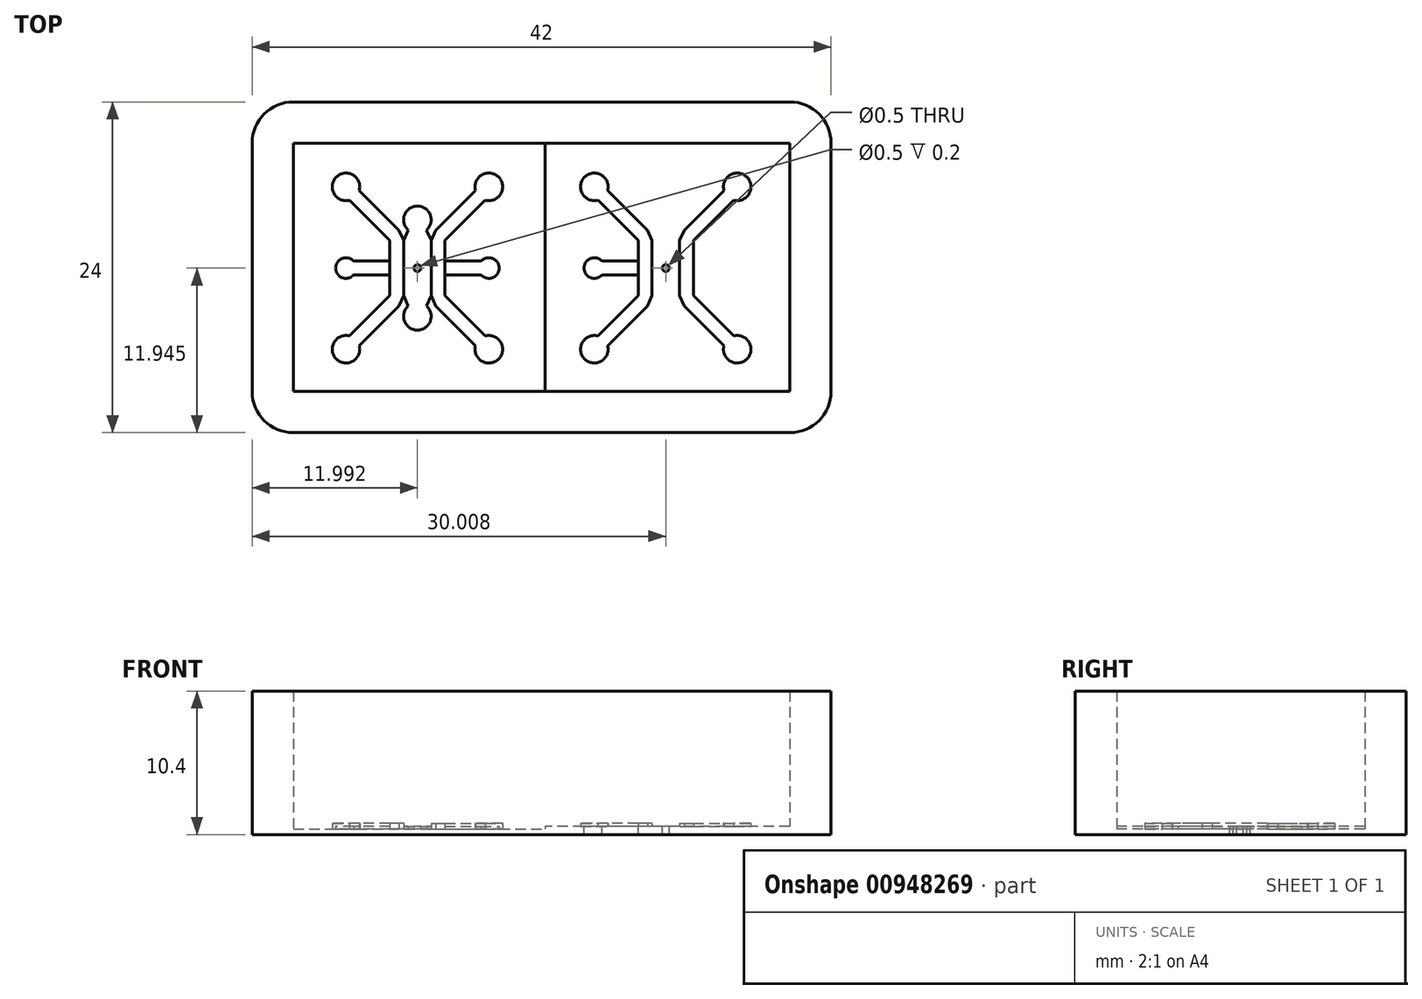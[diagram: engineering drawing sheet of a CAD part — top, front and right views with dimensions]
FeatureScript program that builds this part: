
annotation { "Feature Type Name" : "Feature", "Feature Type Description" : "" }
export const myFeature = defineFeature(function(context is Context, id is Id, definition is map)
    precondition{}
    {
        {
            var Q0;
            Q0=qCreatedBy(makeId("Top.planeOp"),FACE);
            var sketch = newSketch(context, id + "F0", { "sketchPlane" : qUnion([Q0])});
            skLineSegment(sketch, "E0.right", {"start": v(10, 8.95) * mm, "end": v(10, 10.95) * mm});
            skLineSegment(sketch, "E1.MirrorCS", {"start": v(8, 8.95) * mm, "end": v(8, 10.95) * mm});
            skLineSegment(sketch, "E2.MirrorCS", {"start": v(10, 8.95) * mm, "end": v(10, 6.95) * mm});
            skLineSegment(sketch, "E3.MirrorCS", {"start": v(8, 8.95) * mm, "end": v(8, 6.95) * mm});
            skLineSegment(sketch, "E4", {"start": v(9.65, 6.2) * mm, "end": v(10, 6.95) * mm});
            skLineSegment(sketch, "E5", {"start": v(8, 6.95) * mm, "end": v(8.33, 6.2) * mm});
            skCircle(sketch, "E6", {"center": v(9, 8.95) * mm, "radius": 0.25 * mm});
            skArc(sketch, "E7", {"start": v(8.33, 6.2) * mm, "mid": v(9, 4.45) * mm, "end": v(9.65, 6.2) * mm});
            skLineSegment(sketch, "E8.left", {"start": v(10, 10.95) * mm, "end": v(10, 8.95) * mm});
            skLineSegment(sketch, "E8.right", {"start": v(11, 10.95) * mm, "end": v(11, 8.95) * mm});
            skLineSegment(sketch, "E9.MirrorCS", {"start": v(11, 6.95) * mm, "end": v(11, 8.95) * mm});
            skLineSegment(sketch, "E10", {"start": v(10, 6.95) * mm, "end": v(10.33, 6.2) * mm});
            skLineSegment(sketch, "E11", {"start": v(10.33, 6.2) * mm, "end": v(11, 5.53) * mm});
            skLineSegment(sketch, "E12", {"start": v(11, 5.53) * mm, "end": v(13.2, 3.32) * mm});
            skArc(sketch, "E13", {"start": v(13.2, 3.32) * mm, "mid": v(14.88, 2.35) * mm, "end": v(13.92, 4.02) * mm});
            skArc(sketch, "E14.MirrorCS", {"start": v(8.33, 11.7) * mm, "mid": v(9, 13.45) * mm, "end": v(9.65, 11.7) * mm});
            skLineSegment(sketch, "E15.MirrorCS", {"start": v(9.65, 11.7) * mm, "end": v(10, 10.95) * mm});
            skLineSegment(sketch, "E16.MirrorCS", {"start": v(8, 10.95) * mm, "end": v(8.33, 11.7) * mm});
            skLineSegment(sketch, "E17.MirrorCS", {"start": v(10, 10.95) * mm, "end": v(10.33, 11.7) * mm});
            skLineSegment(sketch, "E18.MirrorCS", {"start": v(10.33, 11.7) * mm, "end": v(11, 12.36) * mm});
            skLineSegment(sketch, "E19.MirrorCS", {"start": v(11, 12.36) * mm, "end": v(13.2, 14.58) * mm});
            skArc(sketch, "E20.MirrorCS", {"start": v(13.2, 14.58) * mm, "mid": v(14.88, 15.54) * mm, "end": v(13.92, 13.87) * mm});
            skLineSegment(sketch, "E21", {"start": v(11, 6.95) * mm, "end": v(13.92, 4.02) * mm});
            skLineSegment(sketch, "E22.MirrorCS", {"start": v(11, 10.95) * mm, "end": v(13.92, 13.87) * mm});
            skLineSegment(sketch, "E23.MirrorCS", {"start": v(8, 10.95) * mm, "end": v(7.65, 11.7) * mm});
            skLineSegment(sketch, "E24.MirrorCS", {"start": v(8, 6.95) * mm, "end": v(7.65, 6.2) * mm});
            skLineSegment(sketch, "E25.MirrorCS", {"start": v(7.65, 11.7) * mm, "end": v(7, 12.36) * mm});
            skLineSegment(sketch, "E26.MirrorCS", {"start": v(7, 12.36) * mm, "end": v(4.78, 14.58) * mm});
            skArc(sketch, "E27.MirrorCS", {"start": v(4.78, 14.58) * mm, "mid": v(3.1, 15.54) * mm, "end": v(4.07, 13.87) * mm});
            skLineSegment(sketch, "E28.MirrorCS", {"start": v(7, 10.95) * mm, "end": v(4.07, 13.87) * mm});
            skLineSegment(sketch, "E29.MirrorCS", {"start": v(7, 10.95) * mm, "end": v(7, 8.95) * mm});
            skLineSegment(sketch, "E30.MirrorCS", {"start": v(7, 6.95) * mm, "end": v(7, 8.95) * mm});
            skArc(sketch, "E31.MirrorCS", {"start": v(4.78, 3.32) * mm, "mid": v(3.1, 2.35) * mm, "end": v(4.07, 4.02) * mm});
            skLineSegment(sketch, "E32.MirrorCS", {"start": v(7, 6.95) * mm, "end": v(4.07, 4.02) * mm});
            skLineSegment(sketch, "E33.MirrorCS", {"start": v(7, 5.53) * mm, "end": v(4.78, 3.32) * mm});
            skLineSegment(sketch, "E34.MirrorCS", {"start": v(7.65, 6.2) * mm, "end": v(7, 5.53) * mm});
            skLineSegment(sketch, "E35", {"start": v(11, 9.45) * mm, "end": v(13.61, 9.45) * mm});
            skLineSegment(sketch, "E36", {"start": v(11, 8.45) * mm, "end": v(13.61, 8.45) * mm});
            skArc(sketch, "E37", {"start": v(13.8, 9.6) * mm, "mid": v(13.7, 9.53) * mm, "end": v(13.61, 9.45) * mm});
            skArc(sketch, "E38", {"start": v(13.61, 8.45) * mm, "mid": v(14.91, 8.82) * mm, "end": v(13.8, 9.6) * mm});
            skLineSegment(sketch, "E39.MirrorCS", {"start": v(7, 9.45) * mm, "end": v(4.37, 9.45) * mm});
            skLineSegment(sketch, "E40.MirrorCS", {"start": v(7, 8.45) * mm, "end": v(4.37, 8.45) * mm});
            skArc(sketch, "E41.MirrorCS", {"start": v(4.37, 8.45) * mm, "mid": v(3.07, 8.82) * mm, "end": v(4.18, 9.6) * mm});
            skArc(sketch, "E42.MirrorCS", {"start": v(4.18, 9.6) * mm, "mid": v(4.28, 9.53) * mm, "end": v(4.37, 9.45) * mm});
            skPoint(sketch, "E43.startSnap0", {"position": v(15, 8.95) * mm});
            skPoint(sketch, "E43.startSnap1", {"position": v(14.91, 8.82) * mm});
            skPoint(sketch, "E43.endSnap0", {"position": v(14.91, 8.82) * mm});
            skPoint(sketch, "E44.visualSharp", {"position": v(0, 18) * mm});
            skPoint(sketch, "E45.visualSharp", {"position": v(0, 0) * mm});
            skLineSegment(sketch, "E46", {"start": v(9, 12.45) * mm, "end": v(9, 5.45) * mm});
            skLineSegment(sketch, "E47.bottom", {"start": v(0, 18) * mm, "end": v(18, 18) * mm});
            skLineSegment(sketch, "E47.top", {"start": v(0, 0) * mm, "end": v(18, 0) * mm});
            skLineSegment(sketch, "E47.left", {"start": v(0, 18) * mm, "end": v(0, 0) * mm});
            skLineSegment(sketch, "E47.right", {"start": v(18, 18) * mm, "end": v(18, 0) * mm});
            skLineSegment(sketch, "E48", {"start": v(21.4, 0) * mm, "end": v(21.4, 0) * mm});
            skLineSegment(sketch, "E49.MirrorCS", {"start": v(36, 18) * mm, "end": v(36, 0) * mm});
            skPoint(sketch, "E50.MirrorP", {"position": v(36, 0) * mm});
            skLineSegment(sketch, "E51.MirrorCS", {"start": v(36, 18) * mm, "end": v(18, 18) * mm});
            skPoint(sketch, "E52.MirrorP", {"position": v(36, 18) * mm});
            skLineSegment(sketch, "E53.MirrorCS", {"start": v(14.6, 0) * mm, "end": v(14.6, 0) * mm});
            skLineSegment(sketch, "E54.MirrorCS", {"start": v(36, 0) * mm, "end": v(18, 0) * mm});
            skPoint(sketch, "E55.MirrorP", {"position": v(21.09, 8.82) * mm});
            skLineSegment(sketch, "E56.MirrorCS", {"start": v(28, 10.95) * mm, "end": v(27.67, 11.7) * mm});
            skLineSegment(sketch, "E57.MirrorCS", {"start": v(26, 6.95) * mm, "end": v(25.67, 6.2) * mm});
            skLineSegment(sketch, "E58.MirrorCS", {"start": v(26, 8.95) * mm, "end": v(26, 10.95) * mm});
            skLineSegment(sketch, "E59.MirrorCS", {"start": v(28.35, 6.2) * mm, "end": v(29, 5.53) * mm});
            skArc(sketch, "E60.MirrorCS", {"start": v(31.82, 9.6) * mm, "mid": v(31.72, 9.53) * mm, "end": v(31.63, 9.45) * mm});
            skArc(sketch, "E61.MirrorCS", {"start": v(22.2, 9.6) * mm, "mid": v(22.3, 9.53) * mm, "end": v(22.39, 9.45) * mm});
            skLineSegment(sketch, "E62.MirrorCS", {"start": v(25.67, 11.7) * mm, "end": v(25, 12.36) * mm});
            skLineSegment(sketch, "E63.MirrorCS", {"start": v(28, 10.95) * mm, "end": v(28.35, 11.7) * mm});
            skLineSegment(sketch, "E64.MirrorCS", {"start": v(26, 10.95) * mm, "end": v(25.67, 11.7) * mm});
            skLineSegment(sketch, "E65.MirrorCS", {"start": v(26.35, 11.7) * mm, "end": v(26, 10.95) * mm});
            skLineSegment(sketch, "E66.MirrorCS", {"start": v(28.35, 11.7) * mm, "end": v(29, 12.36) * mm});
            skLineSegment(sketch, "E67.MirrorCS", {"start": v(25.67, 6.2) * mm, "end": v(25, 5.53) * mm});
            skLineSegment(sketch, "E68.MirrorCS", {"start": v(28, 6.95) * mm, "end": v(27.67, 6.2) * mm});
            skLineSegment(sketch, "E69.MirrorCS", {"start": v(28, 6.95) * mm, "end": v(28.35, 6.2) * mm});
            skArc(sketch, "E70.MirrorCS", {"start": v(22.39, 8.45) * mm, "mid": v(21.09, 8.82) * mm, "end": v(22.2, 9.6) * mm});
            skLineSegment(sketch, "E71.MirrorCS", {"start": v(26.35, 6.2) * mm, "end": v(26, 6.95) * mm});
            skPoint(sketch, "E72.MirrorP", {"position": v(21, 8.95) * mm});
            skCircle(sketch, "E73.MirrorC", {"center": v(27, 8.95) * mm, "radius": 0.25 * mm});
            skLineSegment(sketch, "E74.MirrorCS", {"start": v(28, 8.95) * mm, "end": v(28, 10.95) * mm});
            skArc(sketch, "E75.MirrorCS", {"start": v(22.8, 14.58) * mm, "mid": v(21.12, 15.54) * mm, "end": v(22.08, 13.87) * mm});
            skLineSegment(sketch, "E76.MirrorCS", {"start": v(29, 9.45) * mm, "end": v(31.63, 9.45) * mm});
            skLineSegment(sketch, "E77.MirrorCS", {"start": v(29, 6.95) * mm, "end": v(31.93, 4.02) * mm});
            skLineSegment(sketch, "E78.MirrorCS", {"start": v(25, 5.53) * mm, "end": v(22.8, 3.32) * mm});
            skLineSegment(sketch, "E79.MirrorCS", {"start": v(27, 12.45) * mm, "end": v(27, 5.45) * mm});
            skLineSegment(sketch, "E80.MirrorCS", {"start": v(29, 12.36) * mm, "end": v(31.22, 14.58) * mm});
            skLineSegment(sketch, "E81.MirrorCS", {"start": v(29, 6.95) * mm, "end": v(29, 8.95) * mm});
            skLineSegment(sketch, "E82.MirrorCS", {"start": v(29, 5.53) * mm, "end": v(31.22, 3.32) * mm});
            skLineSegment(sketch, "E83.MirrorCS", {"start": v(29, 8.45) * mm, "end": v(31.63, 8.45) * mm});
            skLineSegment(sketch, "E84.MirrorCS", {"start": v(29, 10.95) * mm, "end": v(29, 8.95) * mm});
            skLineSegment(sketch, "E85.MirrorCS", {"start": v(25, 12.36) * mm, "end": v(22.8, 14.58) * mm});
            skLineSegment(sketch, "E86.MirrorCS", {"start": v(26, 10.95) * mm, "end": v(26, 8.95) * mm});
            skArc(sketch, "E87.MirrorCS", {"start": v(31.63, 8.45) * mm, "mid": v(32.93, 8.82) * mm, "end": v(31.82, 9.6) * mm});
            skLineSegment(sketch, "E88.MirrorCS", {"start": v(29, 10.95) * mm, "end": v(31.93, 13.87) * mm});
            skLineSegment(sketch, "E89.MirrorCS", {"start": v(28, 8.95) * mm, "end": v(28, 6.95) * mm});
            skLineSegment(sketch, "E90.MirrorCS", {"start": v(25, 6.95) * mm, "end": v(25, 8.95) * mm});
            skArc(sketch, "E91.MirrorCS", {"start": v(22.8, 3.32) * mm, "mid": v(21.12, 2.35) * mm, "end": v(22.08, 4.02) * mm});
            skLineSegment(sketch, "E92.MirrorCS", {"start": v(25, 10.95) * mm, "end": v(22.08, 13.87) * mm});
            skArc(sketch, "E93.MirrorCS", {"start": v(31.22, 14.58) * mm, "mid": v(32.9, 15.54) * mm, "end": v(31.93, 13.87) * mm});
            skLineSegment(sketch, "E94.MirrorCS", {"start": v(26, 8.95) * mm, "end": v(26, 6.95) * mm});
            skArc(sketch, "E95.MirrorCS", {"start": v(31.22, 3.32) * mm, "mid": v(32.9, 2.35) * mm, "end": v(31.93, 4.02) * mm});
            skLineSegment(sketch, "E96.MirrorCS", {"start": v(25, 10.95) * mm, "end": v(25, 8.95) * mm});
            skArc(sketch, "E97.MirrorCS", {"start": v(27.67, 11.7) * mm, "mid": v(27, 13.45) * mm, "end": v(26.35, 11.7) * mm});
            skLineSegment(sketch, "E98.MirrorCS", {"start": v(25, 8.45) * mm, "end": v(22.39, 8.45) * mm});
            skLineSegment(sketch, "E99.MirrorCS", {"start": v(25, 9.45) * mm, "end": v(22.39, 9.45) * mm});
            skLineSegment(sketch, "E100.MirrorCS", {"start": v(25, 6.95) * mm, "end": v(22.08, 4.02) * mm});
            skArc(sketch, "E101.MirrorCS", {"start": v(27.67, 6.2) * mm, "mid": v(27, 4.45) * mm, "end": v(26.35, 6.2) * mm});
            skLineSegment(sketch, "E102", {"start": v(17.75, 18) * mm, "end": v(17.75, 0) * mm});
            skLineSegment(sketch, "E103.MirrorCS", {"start": v(18.25, 18) * mm, "end": v(18.25, 0) * mm});
            skLineSegment(sketch, "E104", {"start": v(0, 21) * mm, "end": v(36, 21) * mm});
            skLineSegment(sketch, "E105", {"start": v(39, 18) * mm, "end": v(39, 0) * mm});
            skLineSegment(sketch, "E106", {"start": v(0, -3) * mm, "end": v(0, -3) * mm});
            skLineSegment(sketch, "E107", {"start": v(-3, 18) * mm, "end": v(-3, 0) * mm});
            skArc(sketch, "E108", {"start": v(0, 21) * mm, "mid": v(-2.12, 20.12) * mm, "end": v(-3, 18) * mm});
            skArc(sketch, "E109", {"start": v(39, 18) * mm, "mid": v(38.12, 20.12) * mm, "end": v(36, 21) * mm});
            skArc(sketch, "E110", {"start": v(36, -3) * mm, "mid": v(38.12, -2.12) * mm, "end": v(39, 0) * mm});
            skLineSegment(sketch, "E111", {"start": v(0, -3) * mm, "end": v(36, -3) * mm});
            skArc(sketch, "E112", {"start": v(-3, 0) * mm, "mid": v(-2.12, -2.12) * mm, "end": v(0, -3) * mm});
            skSolve(sketch);
        }
        {
            var Q0;
            {var subQ0=sQuery(id+"F0.wireOp",EDGE,"E39.MirrorCS");Q0=makeQuery(id+"F0.imprint","IMPRINT",FACE,{"disambiguationData":[TD([[makeQuery(id+"F0.imprint","IMPRINT",EDGE,{"derivedFrom":subQ0}),1.0]])]});}
            var Q1;
            Q1=makeQuery(id+"F0.imprint","IMPRINT",FACE,{"disambiguationData":[TD([[makeQuery(id+"F0.imprint","IMPRINT",EDGE,{"derivedFrom":sQuery(id+"F0.wireOp",EDGE,"E56.MirrorCS")}),1.0]])]});
            var Q2;
            Q2=makeQuery(id+"F0.imprint","IMPRINT",FACE,{"disambiguationData":[TD([[makeQuery(id+"F0.imprint","IMPRINT",EDGE,{"derivedFrom":sQuery(id+"F0.wireOp",EDGE,"E4")}),-1.0]])]});
            var Q3;
            Q3=makeQuery(id+"F0.imprint","IMPRINT",FACE,{"disambiguationData":[TD([[makeQuery(id+"F0.imprint","IMPRINT",EDGE,{"derivedFrom":sQuery(id+"F0.wireOp",EDGE,"E60.MirrorCS")}),1.0]])]});
            var Q4;
            Q4=makeQuery(id+"F0.imprint","IMPRINT",FACE,{"disambiguationData":[TD([[makeQuery(id+"F0.imprint","IMPRINT",EDGE,{"derivedFrom":sQuery(id+"F0.wireOp",EDGE,"E61.MirrorCS")}),-1.0]])]});
            var Q5;
            Q5=makeQuery(id+"F0.imprint","IMPRINT",FACE,{"disambiguationData":[TD([[makeQuery(id+"F0.imprint","IMPRINT",EDGE,{"derivedFrom":sQuery(id+"F0.wireOp",EDGE,"E57.MirrorCS")}),-1.0]])]});
            var Q6;
            {var subQ1=sQuery(id+"F0.wireOp",EDGE,"E49.MirrorCS");Q6=makeQuery(id+"F0.imprint","IMPRINT",FACE,{"disambiguationData":[TD([[makeQuery(id+"F0.imprint","IMPRINT",EDGE,{"derivedFrom":subQ1}),-1.0]])]});}
            var Q7;
            Q7=makeQuery(id+"F0.imprint","IMPRINT",FACE,{"disambiguationData":[TD([[makeQuery(id+"F0.imprint","IMPRINT",EDGE,{"derivedFrom":sQuery(id+"F0.wireOp",EDGE,"E59.MirrorCS")}),1.0]])]});
            var Q8;
            Q8=makeQuery(id+"F0.imprint","IMPRINT",FACE,{"disambiguationData":[TD([[makeQuery(id+"F0.imprint","IMPRINT",EDGE,{"derivedFrom":sQuery(id+"F0.wireOp",EDGE,"E1.MirrorCS")}),1.0]])]});
            var Q9;
            Q9=makeQuery(id+"F0.imprint","IMPRINT",FACE,{"disambiguationData":[TD([[makeQuery(id+"F0.imprint","IMPRINT",EDGE,{"derivedFrom":sQuery(id+"F0.wireOp",EDGE,"E2.MirrorCS")}),1.0]])]});
            var Q10;
            Q10=makeQuery(id+"F0.imprint","IMPRINT",FACE,{"disambiguationData":[TD([[makeQuery(id+"F0.imprint","IMPRINT",EDGE,{"derivedFrom":sQuery(id+"F0.wireOp",EDGE,"E1.MirrorCS")}),-1.0]])]});
            var Q11;
            {var subQ4=sQuery(id+"F0.wireOp",EDGE,"E35");Q11=makeQuery(id+"F0.imprint","IMPRINT",FACE,{"disambiguationData":[TD([[makeQuery(id+"F0.imprint","IMPRINT",EDGE,{"derivedFrom":subQ4}),-1.0]])]});}
            var Q12;
            {var subQ3=sQuery(id+"F0.wireOp",EDGE,"E102");Q12=makeQuery(id+"F0.imprint","IMPRINT",FACE,{"disambiguationData":[TD([[makeQuery(id+"F0.imprint","IMPRINT",EDGE,{"derivedFrom":subQ3}),1.0]])]});}
            var Q13;
            {var subQ5=sQuery(id+"F0.wireOp",EDGE,"E103.MirrorCS");Q13=makeQuery(id+"F0.imprint","IMPRINT",FACE,{"disambiguationData":[TD([[makeQuery(id+"F0.imprint","IMPRINT",EDGE,{"derivedFrom":subQ5}),-1.0]])]});}
            var Q14;
            {var subQ0=sQuery(id+"F0.wireOp",EDGE,"E46");var subQ1=sQuery(id+"F0.wireOp",EDGE,"E6");var subQ2=makeQuery(id+"F0.imprint","INTERSECT",VERTEX,{"disambiguationData":[OD(0.0)],"derivedFrom":[subQ1,subQ0]});Q14=makeQuery(id+"F0.imprint","IMPRINT",FACE,{"disambiguationData":[TD([[makeQuery(id+"F0.imprint","IMPRINT",EDGE,{"disambiguationData":[TD([[subQ2,1.0]])],"derivedFrom":subQ1}),1.0]])]});}
            var Q15;
            {var subQ0=sQuery(id+"F0.wireOp",EDGE,"E79.MirrorCS");var subQ1=sQuery(id+"F0.wireOp",EDGE,"E73.MirrorC");var subQ2=makeQuery(id+"F0.imprint","INTERSECT",VERTEX,{"disambiguationData":[OD(0.0)],"derivedFrom":[subQ1,subQ0]});Q15=makeQuery(id+"F0.imprint","IMPRINT",FACE,{"disambiguationData":[TD([[makeQuery(id+"F0.imprint","IMPRINT",EDGE,{"disambiguationData":[TD([[subQ2,1.0]])],"derivedFrom":subQ1}),-1.0]])]});}
            var Q16;
            {var subQ0=sQuery(id+"F0.wireOp",EDGE,"E46");var subQ1=sQuery(id+"F0.wireOp",EDGE,"E6");var subQ2=makeQuery(id+"F0.imprint","INTERSECT",VERTEX,{"disambiguationData":[OD(0.0)],"derivedFrom":[subQ1,subQ0]});Q16=makeQuery(id+"F0.imprint","IMPRINT",FACE,{"disambiguationData":[TD([[makeQuery(id+"F0.imprint","IMPRINT",EDGE,{"disambiguationData":[TD([[subQ2,-1.0]])],"derivedFrom":subQ1}),1.0]])]});}
            var Q17;
            {var subQ0=sQuery(id+"F0.wireOp",EDGE,"E79.MirrorCS");var subQ1=sQuery(id+"F0.wireOp",EDGE,"E73.MirrorC");var subQ2=makeQuery(id+"F0.imprint","INTERSECT",VERTEX,{"disambiguationData":[OD(0.0)],"derivedFrom":[subQ1,subQ0]});Q17=makeQuery(id+"F0.imprint","IMPRINT",FACE,{"disambiguationData":[TD([[makeQuery(id+"F0.imprint","IMPRINT",EDGE,{"disambiguationData":[TD([[subQ2,-1.0]])],"derivedFrom":subQ1}),-1.0]])]});}
            var Q18;
            {var subQ0=sQuery(id+"F0.wireOp",EDGE,"E51.MirrorCS");var subQ1=sQuery(id+"F0.wireOp",EDGE,"E47.bottom");var subQ2=makeQuery(id+"F0.imprint","INTERSECT",VERTEX,{"derivedFrom":[subQ1,sQuery(id+"F0.wireOp",EDGE,"E47.right"),subQ0]});Q18=makeQuery(id+"F0.imprint","IMPRINT",FACE,{"disambiguationData":[TD([[makeQuery(id+"F0.imprint","IMPRINT",EDGE,{"disambiguationData":[TD([[subQ2,1.0]])],"derivedFrom":subQ1}),1.0]])]});}
            var Q19;
            {var subQ0=sQuery(id+"F0.wireOp",EDGE,"E47.right");var subQ3=sQuery(id+"F0.wireOp",EDGE,"8D0ttMVF-N7t8-bLoh-d2Lt-IWmziKVZ8kqY");var subQ5=makeQuery(id+"F0.imprint","INTERSECT",VERTEX,{"derivedFrom":[subQ0,subQ3]});Q19=makeQuery(id+"F0.imprint","IMPRINT",FACE,{"disambiguationData":[TD([[makeQuery(id+"F0.imprint","IMPRINT",EDGE,{"disambiguationData":[TD([[subQ5,1.0]])],"derivedFrom":subQ0}),-1.0]])]});}
            var Q20;
            {var subQ1=sQuery(id+"F0.wireOp",EDGE,"E47.right");var subQ3=sQuery(id+"F0.wireOp",EDGE,"8D0ttMVF-N7t8-bLoh-d2Lt-IWmziKVZ8kqY");var subQ4=makeQuery(id+"F0.imprint","INTERSECT",VERTEX,{"derivedFrom":[subQ1,subQ3]});Q20=makeQuery(id+"F0.imprint","IMPRINT",FACE,{"disambiguationData":[TD([[makeQuery(id+"F0.imprint","IMPRINT",EDGE,{"disambiguationData":[TD([[subQ4,1.0]])],"derivedFrom":subQ1}),1.0]])]});}
            extrude(context, id + "F1", {"entities" : qUnion([Q0, Q1, Q2, Q3, Q4, Q5, Q6, Q7, Q8, Q9, Q10, Q11, Q12, Q13, Q14, Q15, Q16, Q17, Q18, Q19, Q20]), "depth" : -0.4 * mm, "offsetDistance" : 25 * mm});
        }
        {
            var Q0;
            {var subQ11=sQuery(id+"F0.wireOp",EDGE,"E47.left");Q0=makeQuery(id+"F0.imprint","IMPRINT",FACE,{"disambiguationData":[TD([[makeQuery(id+"F0.imprint","IMPRINT",EDGE,{"derivedFrom":subQ11}),-1.0]])]});}
            extrude(context, id + "F2", {"entities" : qUnion([Q0]), "operationType" : NewBodyOperationType.ADD, "depth" : 10 * mm, "offsetDistance" : 25 * mm});
        }
        {
            var Q0;
            Q0=makeQuery(id+"F0.imprint","IMPRINT",FACE,{"disambiguationData":[TD([[makeQuery(id+"F0.imprint","IMPRINT",EDGE,{"derivedFrom":sQuery(id+"F0.wireOp",EDGE,"E1.MirrorCS")}),-1.0]])]});
            var Q1;
            {var subQ4=sQuery(id+"F0.wireOp",EDGE,"E35");Q1=makeQuery(id+"F0.imprint","IMPRINT",FACE,{"disambiguationData":[TD([[makeQuery(id+"F0.imprint","IMPRINT",EDGE,{"derivedFrom":subQ4}),-1.0]])]});}
            var Q2;
            {var subQ0=sQuery(id+"F0.wireOp",EDGE,"E39.MirrorCS");Q2=makeQuery(id+"F0.imprint","IMPRINT",FACE,{"disambiguationData":[TD([[makeQuery(id+"F0.imprint","IMPRINT",EDGE,{"derivedFrom":subQ0}),1.0]])]});}
            var Q3;
            Q3=makeQuery(id+"F0.imprint","IMPRINT",FACE,{"disambiguationData":[TD([[makeQuery(id+"F0.imprint","IMPRINT",EDGE,{"derivedFrom":sQuery(id+"F0.wireOp",EDGE,"E61.MirrorCS")}),-1.0]])]});
            var Q4;
            Q4=makeQuery(id+"F0.imprint","IMPRINT",FACE,{"disambiguationData":[TD([[makeQuery(id+"F0.imprint","IMPRINT",EDGE,{"derivedFrom":sQuery(id+"F0.wireOp",EDGE,"E56.MirrorCS")}),1.0]])]});
            var Q5;
            Q5=makeQuery(id+"F0.imprint","IMPRINT",FACE,{"disambiguationData":[TD([[makeQuery(id+"F0.imprint","IMPRINT",EDGE,{"derivedFrom":sQuery(id+"F0.wireOp",EDGE,"E60.MirrorCS")}),1.0]])]});
            extrude(context, id + "F3", {"entities" : qUnion([Q0, Q1, Q2, Q3, Q4, Q5]), "operationType" : NewBodyOperationType.ADD, "depth" : .2 * mm, "offsetDistance" : 25 * mm});
        }
        {
            var Q0;
            Q0=makeQuery(id+"F0.imprint","IMPRINT",FACE,{"disambiguationData":[TD([[makeQuery(id+"F0.imprint","IMPRINT",EDGE,{"derivedFrom":sQuery(id+"F0.wireOp",EDGE,"E1.MirrorCS")}),1.0]])]});
            var Q1;
            Q1=makeQuery(id+"F0.imprint","IMPRINT",FACE,{"disambiguationData":[TD([[makeQuery(id+"F0.imprint","IMPRINT",EDGE,{"derivedFrom":sQuery(id+"F0.wireOp",EDGE,"E2.MirrorCS")}),1.0]])]});
            var Q2;
            Q2=makeQuery(id+"F0.imprint","IMPRINT",FACE,{"disambiguationData":[TD([[makeQuery(id+"F0.imprint","IMPRINT",EDGE,{"derivedFrom":sQuery(id+"F0.wireOp",EDGE,"E57.MirrorCS")}),-1.0]])]});
            var Q3;
            Q3=makeQuery(id+"F0.imprint","IMPRINT",FACE,{"disambiguationData":[TD([[makeQuery(id+"F0.imprint","IMPRINT",EDGE,{"derivedFrom":sQuery(id+"F0.wireOp",EDGE,"E59.MirrorCS")}),1.0]])]});
            extrude(context, id + "F4", {"entities" : qUnion([Q0, Q1, Q2, Q3]), "operationType" : NewBodyOperationType.ADD, "depth" : .4 * mm, "offsetDistance" : 25 * mm});
        }
    });
